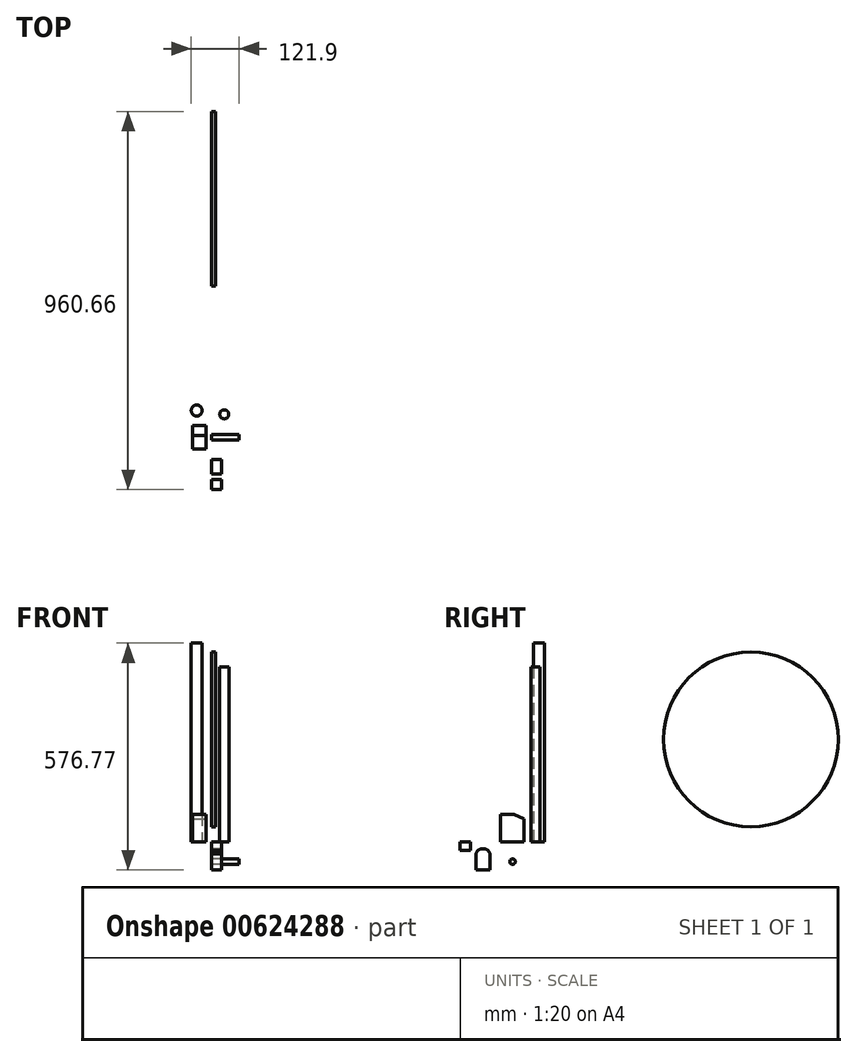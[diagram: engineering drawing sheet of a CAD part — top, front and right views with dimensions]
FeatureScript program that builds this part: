
annotation { "Feature Type Name" : "Feature", "Feature Type Description" : "" }
export const myFeature = defineFeature(function(context is Context, id is Id, definition is map)
    precondition{}
    {
        {
            var Q0;
            Q0=qCreatedBy(makeId("Top.planeOp"),FACE);
            var sketch = newSketch(context, id + "F0", { "sketchPlane" : qUnion([Q0])});
            skCircle(sketch, "E0", {"center": v(-37.9, 29.82) * mm, "radius": 14 * mm});
            skSolve(sketch);
        }
        {
            var Q0;
            Q0=makeQuery(id+"F0.imprint","IMPRINT",FACE,{"disambiguationData":[TD([[makeQuery(id+"F0.imprint","IMPRINT",EDGE,{"derivedFrom":sQuery(id+"F0.wireOp",EDGE,"E0")}),1.0]])]});
            extrude(context, id + "F1", {"entities" : qUnion([Q0]), "depth" : 505 * mm, "offsetDistance" : 25 * mm});
        }
        {
            var Q0;
            Q0=qCreatedBy(makeId("Top.planeOp"),FACE);
            var sketch = newSketch(context, id + "F2", { "sketchPlane" : qUnion([Q0])});
            skCircle(sketch, "E1", {"center": v(32.13, 20.2) * mm, "radius": 11.5 * mm});
            skSolve(sketch);
        }
        {
            var Q0;
            Q0=makeQuery(id+"F2.imprint","IMPRINT",FACE,{"disambiguationData":[TD([[makeQuery(id+"F2.imprint","IMPRINT",EDGE,{"derivedFrom":sQuery(id+"F2.wireOp",EDGE,"E1")}),1.0]])]});
            extrude(context, id + "F3", {"entities" : qUnion([Q0]), "depth" : 445 * mm, "offsetDistance" : 25 * mm});
        }
        {
            var Q0;
            Q0=qCreatedBy(makeId("Top.planeOp"),FACE);
            var sketch = newSketch(context, id + "F4", { "sketchPlane" : qUnion([Q0])});
            skLineSegment(sketch, "E2.bottom", {"start": v(-48.57, -8.22) * mm, "end": v(-13.57, -8.22) * mm});
            skLineSegment(sketch, "E2.top", {"start": v(-48.57, -68.22) * mm, "end": v(-13.57, -68.22) * mm});
            skLineSegment(sketch, "E2.left", {"start": v(-48.57, -8.22) * mm, "end": v(-48.57, -68.22) * mm});
            skLineSegment(sketch, "E2.right", {"start": v(-13.57, -8.22) * mm, "end": v(-13.57, -68.22) * mm});
            skSolve(sketch);
        }
        {
            var Q0;
            Q0=makeQuery(id+"F4.imprint","IMPRINT",FACE,{"disambiguationData":[TD([[makeQuery(id+"F4.imprint","IMPRINT",EDGE,{"derivedFrom":sQuery(id+"F4.wireOp",EDGE,"E2.bottom")}),-1.0]])]});
            extrude(context, id + "F5", {"entities" : qUnion([Q0]), "depth" : 70 * mm, "offsetDistance" : 25 * mm});
        }
        {
            var Q0;
            Q0=makeQuery(id+"F5.opExtrude","CAP_EDGE",EDGE,{"disambiguationData":[OSD([sQuery(id+"F4.wireOp",EDGE,"E2.bottom")])],"isStart":false});
            chamfer(context, id + "F6", {"entities" : qUnion([Q0]), "chamferType" : ChamferType.TWO_OFFSETS, "width1" : 12 * mm, "oppositeDirection" : false, "width2" : 26 * mm, "tangentPropagation" : true});
        }
        {
            var Q0;
            Q0=qCreatedBy(makeId("Right.planeOp"),FACE);
            var sketch = newSketch(context, id + "F7", { "sketchPlane" : qUnion([Q0])});
            skCircle(sketch, "E3", {"center": v(-37.9, -50.22) * mm, "radius": 7 * mm});
            skSolve(sketch);
        }
        {
            var Q0;
            Q0=makeQuery(id+"F7.imprint","IMPRINT",FACE,{"disambiguationData":[TD([[makeQuery(id+"F7.imprint","IMPRINT",EDGE,{"derivedFrom":sQuery(id+"F7.wireOp",EDGE,"E3")}),1.0]])]});
            extrude(context, id + "F8", {"entities" : qUnion([Q0]), "depth" : 70 * mm, "offsetDistance" : 25 * mm});
        }
        {
            var Q0;
            Q0=qCreatedBy(makeId("Right.planeOp"),FACE);
            var sketch = newSketch(context, id + "F9", { "sketchPlane" : qUnion([Q0])});
            skLineSegment(sketch, "E4.top", {"start": v(-131.03, -71.77) * mm, "end": v(-94.86, -71.77) * mm});
            skLineSegment(sketch, "E4.left", {"start": v(-131.03, -30.98) * mm, "end": v(-131.03, -71.77) * mm});
            skLineSegment(sketch, "E4.right", {"start": v(-94.86, -30.98) * mm, "end": v(-94.86, -71.77) * mm});
            skArc(sketch, "E5", {"start": v(-94.86, -30.98) * mm, "mid": v(-112.94, -17.31) * mm, "end": v(-131.03, -30.98) * mm});
            skSolve(sketch);
        }
        {
            var Q0;
            Q0=qCreatedBy(makeId("Right.planeOp"),FACE);
            var sketch = newSketch(context, id + "F10", { "sketchPlane" : qUnion([Q0])});
            skLineSegment(sketch, "E6.bottom", {"start": v(-171.05, 0) * mm, "end": v(-144.88, 0) * mm});
            skLineSegment(sketch, "E6.top", {"start": v(-171.05, -21.74) * mm, "end": v(-144.88, -21.74) * mm});
            skLineSegment(sketch, "E6.left", {"start": v(-171.05, 0) * mm, "end": v(-171.05, -21.74) * mm});
            skLineSegment(sketch, "E6.right", {"start": v(-144.88, 0) * mm, "end": v(-144.88, -21.74) * mm});
            skSolve(sketch);
        }
        {
            var Q0;
            Q0=makeQuery(id+"F9.imprint","IMPRINT",FACE,{"disambiguationData":[TD([[makeQuery(id+"F9.imprint","IMPRINT",EDGE,{"derivedFrom":sQuery(id+"F9.wireOp",EDGE,"E4.top")}),1.0]])]});
            extrude(context, id + "F11", {"entities" : qUnion([Q0]), "depth" : 25 * mm, "offsetDistance" : 25 * mm});
        }
        {
            var Q0;
            Q0=makeQuery(id+"F10.imprint","IMPRINT",FACE,{"disambiguationData":[TD([[makeQuery(id+"F10.imprint","IMPRINT",EDGE,{"derivedFrom":sQuery(id+"F10.wireOp",EDGE,"E6.bottom")}),-1.0]])]});
            extrude(context, id + "F12", {"entities" : qUnion([Q0]), "depth" : 25 * mm, "offsetDistance" : 25 * mm});
        }
        {
            var Q0;
            Q0=qCreatedBy(makeId("Right.planeOp"),FACE);
            var sketch = newSketch(context, id + "F13", { "sketchPlane" : qUnion([Q0])});
            skCircle(sketch, "E7", {"center": v(567.6, 260.38) * mm, "radius": 222 * mm});
            skSolve(sketch);
        }
        {
            var Q0;
            Q0=makeQuery(id+"F13.imprint","IMPRINT",FACE,{"disambiguationData":[TD([[makeQuery(id+"F13.imprint","IMPRINT",EDGE,{"derivedFrom":sQuery(id+"F13.wireOp",EDGE,"E7")}),1.0]])]});
            extrude(context, id + "F14", {"entities" : qUnion([Q0]), "depth" : 10 * mm, "offsetDistance" : 25 * mm});
        }
    });
